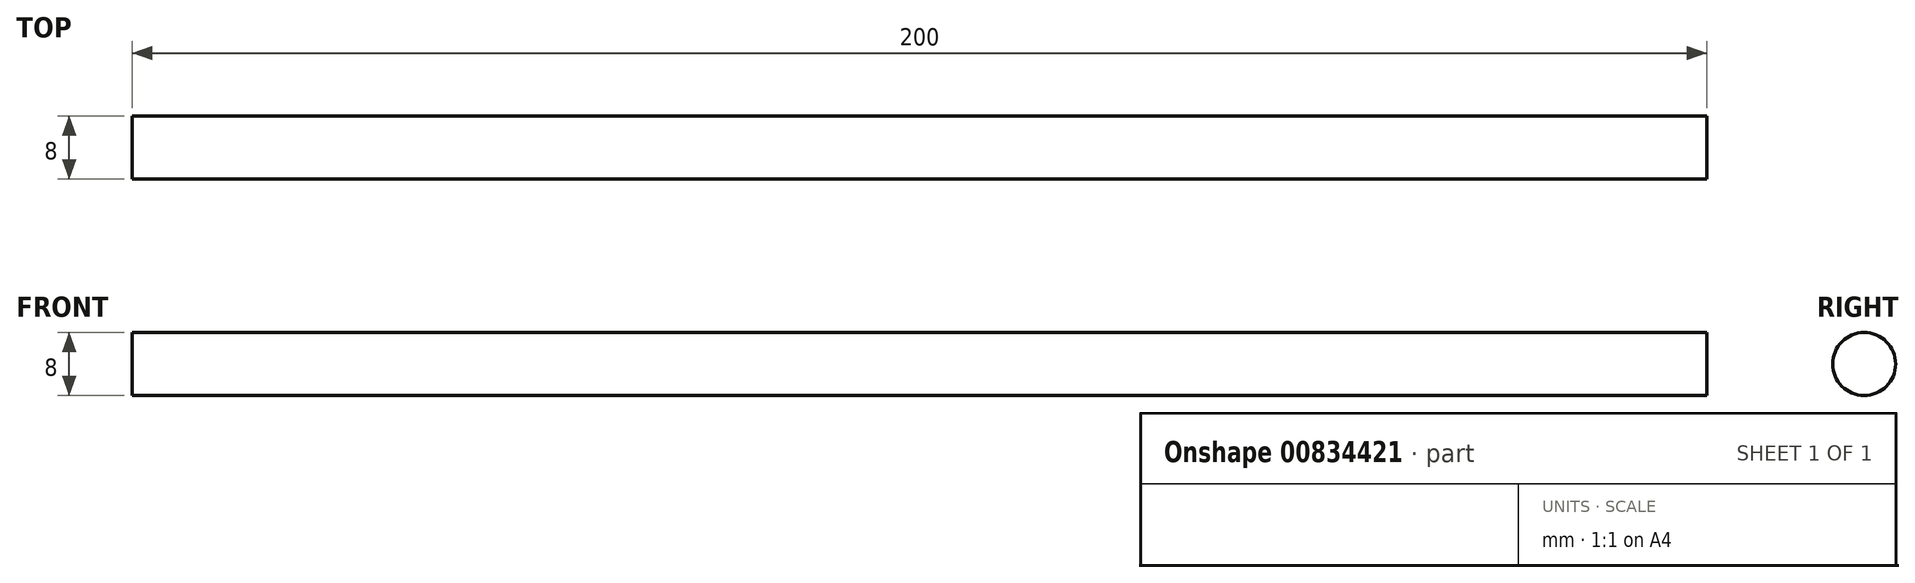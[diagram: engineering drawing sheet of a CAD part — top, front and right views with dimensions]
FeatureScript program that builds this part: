
annotation { "Feature Type Name" : "Feature", "Feature Type Description" : "" }
export const myFeature = defineFeature(function(context is Context, id is Id, definition is map)
    precondition{}
    {
        {
            var Q0;
            Q0=qCreatedBy(makeId("Right.planeOp"),FACE);
            var sketch = newSketch(context, id + "F0", { "sketchPlane" : qUnion([Q0])});
            skCircle(sketch, "E0", {"center": v(0, 0) * mm, "radius": 4 * mm});
            skSolve(sketch);
        }
        {
            var Q0;
            Q0=makeQuery(id+"F0.imprint","IMPRINT",FACE,{"disambiguationData":[TD([[makeQuery(id+"F0.imprint","IMPRINT",EDGE,{"derivedFrom":sQuery(id+"F0.wireOp",EDGE,"E0")}),1.0]])]});
            extrude(context, id + "F1", {"entities" : qUnion([Q0]), "depth" : 200 * mm, "offsetDistance" : 25 * mm});
        }
    });
